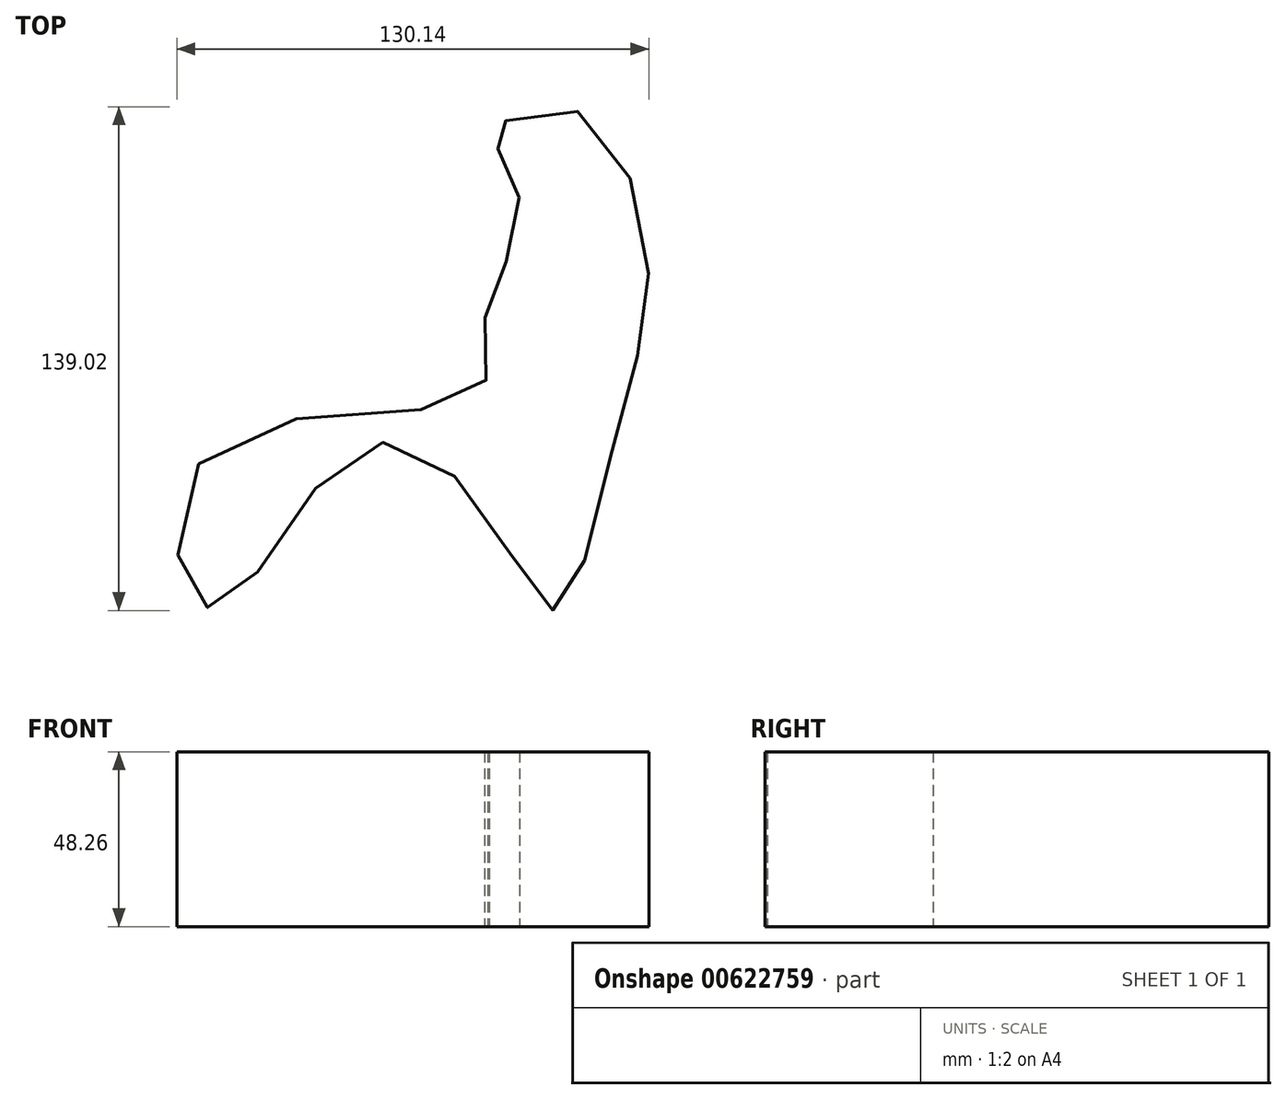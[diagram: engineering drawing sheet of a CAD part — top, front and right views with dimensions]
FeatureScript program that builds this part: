
annotation { "Feature Type Name" : "Feature", "Feature Type Description" : "" }
export const myFeature = defineFeature(function(context is Context, id is Id, definition is map)
    precondition{}
    {
        {
            var Q0;
            Q0=qCreatedBy(makeId("Top.planeOp"),FACE);
            var sketch = newSketch(context, id + "F0", { "sketchPlane" : qUnion([Q0])});
            skFitSpline(sketch, "E0", {"points": [v(17, 10.8) * mm, v(25.3, 32.39) * mm, v(22.92, 55.17) * mm, v(18.2, 60.79) * mm, v(40.38, 68.48) * mm, v(61.97, 27.07) * mm, v(53.4, -20.56) * mm, v(36.83, -69.96) * mm, v(16.42, -42.15) * mm, v(-17, -25) * mm, v(-51.32, -65.81) * mm, v(-63.74, -66.4) * mm, v(-57.53, -25) * mm, v(14.64, -10.5) * mm, v(17, 10.8) * mm]});
            skSolve(sketch);
        }
        {
            var Q0;
            Q0 = qSketchRegion(id + "F0", true);
            extrude(context, id + "F1", {"entities" : qUnion([Q0]), "depth" : 48.26 * mm, "offsetDistance" : 25.4 * mm});
        }
    });
